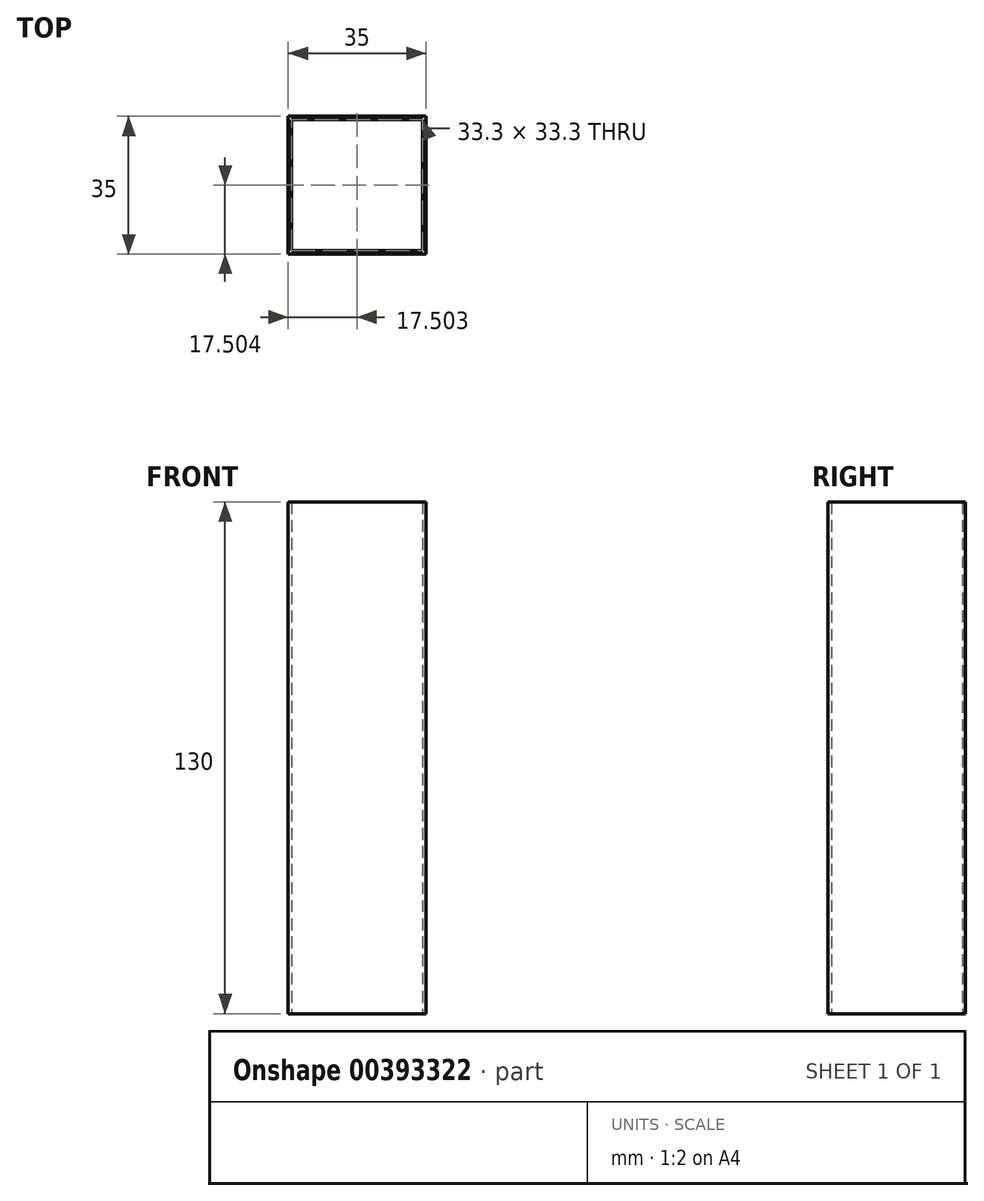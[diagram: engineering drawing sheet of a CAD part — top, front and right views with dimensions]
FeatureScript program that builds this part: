
annotation { "Feature Type Name" : "Feature", "Feature Type Description" : "" }
export const myFeature = defineFeature(function(context is Context, id is Id, definition is map)
    precondition{}
    {
        {
            var Q0;
            Q0=qCreatedBy(makeId("Top.planeOp"),FACE);
            var sketch = newSketch(context, id + "F0", { "sketchPlane" : qUnion([Q0])});
            skLineSegment(sketch, "E0.bottom", {"start": v(-11.72, 12.16) * mm, "end": v(23.28, 12.16) * mm});
            skLineSegment(sketch, "E0.top", {"start": v(-11.72, -22.84) * mm, "end": v(23.28, -22.84) * mm});
            skLineSegment(sketch, "E0.left", {"start": v(-11.72, 12.16) * mm, "end": v(-11.72, -22.84) * mm});
            skLineSegment(sketch, "E0.right", {"start": v(23.28, 12.16) * mm, "end": v(23.28, -22.84) * mm});
            skLineSegment(sketch, "E1.0", {"start": v(-10.87, 11.31) * mm, "end": v(22.43, 11.31) * mm});
            skLineSegment(sketch, "E1.1", {"start": v(-10.87, 11.31) * mm, "end": v(-10.87, -21.99) * mm});
            skLineSegment(sketch, "E1.2", {"start": v(-10.87, -21.99) * mm, "end": v(22.43, -21.99) * mm});
            skLineSegment(sketch, "E1.3", {"start": v(22.43, 11.31) * mm, "end": v(22.43, -21.99) * mm});
            skSolve(sketch);
        }
        {
            var Q0;
            Q0 = qSketchRegion(id + "F0", true);
            extrude(context, id + "F1", {"entities" : qUnion([Q0]), "depth" : 130 * mm});
        }
    });
